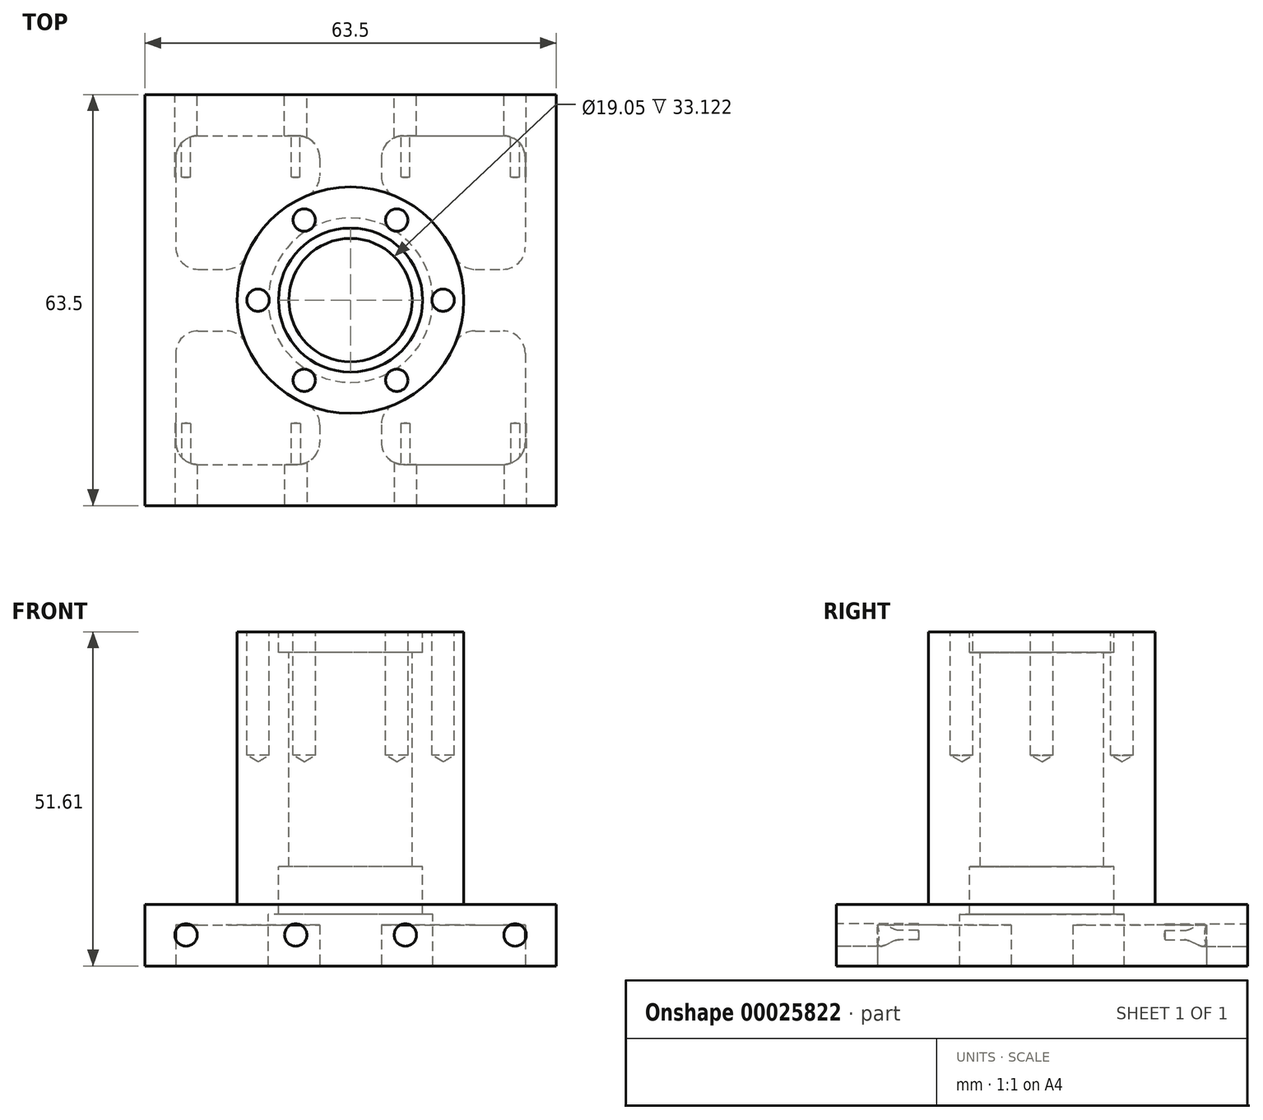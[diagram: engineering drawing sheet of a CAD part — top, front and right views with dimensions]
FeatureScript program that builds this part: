
annotation { "Feature Type Name" : "Feature", "Feature Type Description" : "" }
export const myFeature = defineFeature(function(context is Context, id is Id, definition is map)
    precondition{}
    {
        {
            var Q0;
            Q0=qCreatedBy(makeId("Front.planeOp"),FACE);
            var sketch = newSketch(context, id + "F0", { "sketchPlane" : qUnion([Q0])});
            skLineSegment(sketch, "E0", {"start": v(0, 39.17) * mm, "end": v(0, 0) * mm, "construction": true});
            skLineSegment(sketch, "E1", {"start": v(0, 0) * mm, "end": v(-12.7, 0) * mm, "construction": true});
            skLineSegment(sketch, "E2.bottom", {"start": v(-12.7, 0) * mm, "end": v(-45.72, 0) * mm});
            skLineSegment(sketch, "E2.top", {"start": v(-11.13, 51.61) * mm, "end": v(-17.49, 51.61) * mm});
            skLineSegment(sketch, "E2.left", {"start": v(-9.52, 15.32) * mm, "end": v(-9.53, 48.44) * mm});
            skLineSegment(sketch, "E2.right", {"start": v(-45.72, 0) * mm, "end": v(-45.72, 9.52) * mm});
            skLineSegment(sketch, "E3.top", {"start": v(-11.13, 48.44) * mm, "end": v(-9.53, 48.44) * mm});
            skLineSegment(sketch, "E3.left", {"start": v(-11.13, 51.61) * mm, "end": v(-11.13, 48.44) * mm});
            skLineSegment(sketch, "E4.bottom", {"start": v(-9.53, 15.32) * mm, "end": v(-11.13, 15.32) * mm});
            skLineSegment(sketch, "E4.right", {"start": v(-12.7, 7.95) * mm, "end": v(-12.7, 0) * mm});
            skLineSegment(sketch, "E5.bottom", {"start": v(-11.13, 7.95) * mm, "end": v(-12.7, 7.95) * mm});
            skLineSegment(sketch, "E5.left", {"start": v(-11.13, 7.95) * mm, "end": v(-11.13, 15.32) * mm});
            skLineSegment(sketch, "E6.bottom", {"start": v(-17.49, 9.53) * mm, "end": v(-45.72, 9.52) * mm});
            skLineSegment(sketch, "E6.left", {"start": v(-17.49, 9.53) * mm, "end": v(-17.49, 51.61) * mm});
            skSolve(sketch);
        }
        {
            var Q0;
            Q0=makeQuery(id+"F0.imprint","IMPRINT",FACE,{"disambiguationData":[TD([[makeQuery(id+"F0.imprint","IMPRINT",EDGE,{"derivedFrom":sQuery(id+"F0.wireOp",EDGE,"E2.bottom")}),-1.0]])]});
            var Q1;
            Q1=sQuery(id+"F0.wireOp",EDGE,"E0");
            revolve(context, id + "F1", {"entities" : qUnion([Q0]), "axis" : qUnion([Q1]), "revolveType" : RevolveType.FULL});
        }
        {
            var Q0;
            Q0=makeQuery(id+"F1.opRevolve","SWEPT_FACE",FACE,{"disambiguationData":[OSD([sQuery(id+"F0.wireOp",EDGE,"E2.bottom")])]});
            var sketch = newSketch(context, id + "F2", { "sketchPlane" : qUnion([Q0])});
            skLineSegment(sketch, "E7.rect.bottom", {"start": v(31.75, 31.75) * mm, "end": v(-31.75, 31.75) * mm});
            skLineSegment(sketch, "E7.rect.top", {"start": v(31.75, -31.75) * mm, "end": v(-31.75, -31.75) * mm});
            skLineSegment(sketch, "E7.rect.left", {"start": v(31.75, 31.75) * mm, "end": v(31.75, -31.75) * mm});
            skLineSegment(sketch, "E7.rect.right", {"start": v(-31.75, 31.75) * mm, "end": v(-31.75, -31.75) * mm});
            skPoint(sketch, "E7.rect.middle", {"position": v(0, 0) * mm});
            skSolve(sketch);
        }
        {
            var Q0;
            Q0=makeQuery(id+"F2.imprint","IMPRINT",FACE,{"disambiguationData":[TD([[makeQuery(id+"F2.imprint","IMPRINT",EDGE,{"derivedFrom":sQuery(id+"F2.wireOp",EDGE,"E7.rect.bottom")}),-1.0]])]});
            extrude(context, id + "F3", {"entities" : qUnion([Q0]), "operationType" : NewBodyOperationType.REMOVE, "endBound" : BoundingType.THROUGH_ALL, "oppositeDirection" : true, "depth" : 25.4 * mm});
        }
        {
            var Q0;
            Q0=makeQuery(id+"F3.boolean.opBoolean","COPY",FACE,{"derivedFrom":makeQuery(id+"F3.opExtrude","SWEPT_FACE",FACE,{"disambiguationData":[OSD([sQuery(id+"F2.wireOp",EDGE,"E7.rect.bottom")])]})});
            var sketch = newSketch(context, id + "F4", { "sketchPlane" : qUnion([Q0])});
            skLineSegment(sketch, "E8", {"start": v(-25.4, 4.78) * mm, "end": v(25.4, 4.78) * mm});
            skPoint(sketch, "E9", {"position": v(-8.47, 4.78) * mm});
            skPoint(sketch, "E10", {"position": v(8.47, 4.78) * mm});
            skLineSegment(sketch, "E11", {"start": v(0, 9.52) * mm, "end": v(0, -11.62) * mm});
            skSolve(sketch);
        }
        {
            var Q0;
            Q0=sQuery(id+"F4.wireOp",VERTEX,"E8.start");
            var Q1;
            Q1=sQuery(id+"F4.wireOp",VERTEX,"E9");
            var Q2;
            Q2=sQuery(id+"F4.wireOp",VERTEX,"E10");
            var Q3;
            Q3=sQuery(id+"F4.wireOp",VERTEX,"E8.end");
            var Q4;
            Q4=makeQuery(id+"F1.opRevolve","SWEPT_BODY",BODY,{"disambiguationData":[OSD([sQuery(id+"F0.wireOp",EDGE,"E2.bottom"),sQuery(id+"F0.wireOp",EDGE,"E2.top"),sQuery(id+"F0.wireOp",EDGE,"E2.left"),sQuery(id+"F0.wireOp",EDGE,"E2.right"),sQuery(id+"F0.wireOp",EDGE,"E3.top"),sQuery(id+"F0.wireOp",EDGE,"E3.left"),sQuery(id+"F0.wireOp",EDGE,"E4.bottom"),sQuery(id+"F0.wireOp",EDGE,"E4.right"),sQuery(id+"F0.wireOp",EDGE,"E5.bottom"),sQuery(id+"F0.wireOp",EDGE,"E5.left"),sQuery(id+"F0.wireOp",EDGE,"E6.bottom"),sQuery(id+"F0.wireOp",EDGE,"E6.left")])]});
            hole(context, id + "F5", {"style" : HoleStyle.SIMPLE, "holeDiameter" : 3.45 * mm, "endStyle" : HoleEndStyle.BLIND, "holeDepth" : 12.7 * mm, "locations" : qUnion([Q0, Q1, Q2, Q3]), "scope" : qUnion([Q4])});
        }
        {
            var Q0;
            Q0=makeQuery(id+"F1.opRevolve","SWEPT_FACE",FACE,{"disambiguationData":[OSD([sQuery(id+"F0.wireOp",EDGE,"E2.top")])]});
            var sketch = newSketch(context, id + "F6", { "sketchPlane" : qUnion([Q0])});
            skLineSegment(sketch, "E12", {"start": v(0, 0) * mm, "end": v(14.29, 0) * mm});
            skLineSegment(sketch, "E13.1.0", {"start": v(0, 0) * mm, "end": v(7.14, 12.37) * mm});
            skLineSegment(sketch, "E13.2.0", {"start": v(0, 0) * mm, "end": v(-7.14, 12.37) * mm});
            skLineSegment(sketch, "E13.3.0", {"start": v(0, 0) * mm, "end": v(-14.29, 0) * mm});
            skLineSegment(sketch, "E13.4.0", {"start": v(0, 0) * mm, "end": v(-7.14, -12.37) * mm});
            skLineSegment(sketch, "E13.5.0", {"start": v(0, 0) * mm, "end": v(7.14, -12.37) * mm});
            skPoint(sketch, "E13.center", {"position": v(0, 0) * mm});
            skSolve(sketch);
        }
        {
            var Q0;
            Q0=sQuery(id+"F6.wireOp",VERTEX,"E12.end");
            var Q1;
            Q1=sQuery(id+"F6.wireOp",VERTEX,"E13.5.0.end");
            var Q2;
            Q2=sQuery(id+"F6.wireOp",VERTEX,"E13.4.0.end");
            var Q3;
            Q3=sQuery(id+"F6.wireOp",VERTEX,"E13.3.0.end");
            var Q4;
            Q4=sQuery(id+"F6.wireOp",VERTEX,"E13.2.0.end");
            var Q5;
            Q5=sQuery(id+"F6.wireOp",VERTEX,"E13.1.0.end");
            var Q6;
            Q6=makeQuery(id+"F1.opRevolve","SWEPT_BODY",BODY,{"disambiguationData":[OSD([sQuery(id+"F0.wireOp",EDGE,"E2.bottom"),sQuery(id+"F0.wireOp",EDGE,"E2.top"),sQuery(id+"F0.wireOp",EDGE,"E2.left"),sQuery(id+"F0.wireOp",EDGE,"E2.right"),sQuery(id+"F0.wireOp",EDGE,"E3.top"),sQuery(id+"F0.wireOp",EDGE,"E3.left"),sQuery(id+"F0.wireOp",EDGE,"E4.bottom"),sQuery(id+"F0.wireOp",EDGE,"E4.right"),sQuery(id+"F0.wireOp",EDGE,"E5.bottom"),sQuery(id+"F0.wireOp",EDGE,"E5.left"),sQuery(id+"F0.wireOp",EDGE,"E6.bottom"),sQuery(id+"F0.wireOp",EDGE,"E6.left")])]});
            hole(context, id + "F7", {"style" : HoleStyle.SIMPLE, "holeDiameter" : 3.45 * mm, "endStyle" : HoleEndStyle.BLIND, "holeDepth" : 19.05 * mm, "locations" : qUnion([Q0, Q1, Q2, Q3, Q4, Q5]), "scope" : qUnion([Q6])});
        }
        {
            var Q0;
            Q0=makeQuery(id+"F1.opRevolve","SWEPT_FACE",FACE,{"disambiguationData":[OSD([sQuery(id+"F0.wireOp",EDGE,"E2.bottom")])]});
            var sketch = newSketch(context, id + "F8", { "sketchPlane" : qUnion([Q0])});
            skLineSegment(sketch, "E14.rect.bottom", {"start": v(-26.97, -25.4) * mm, "end": v(-4.76, -25.4) * mm});
            skLineSegment(sketch, "E14.rect.top", {"start": v(-26.97, 25.4) * mm, "end": v(-4.76, 25.4) * mm});
            skLineSegment(sketch, "E14.rect.left", {"start": v(-26.97, -25.4) * mm, "end": v(-26.97, -4.76) * mm});
            skLineSegment(sketch, "E14.rect.right", {"start": v(26.97, -25.4) * mm, "end": v(26.97, -4.76) * mm});
            skPoint(sketch, "E14.rect.middle", {"position": v(0, 0) * mm});
            skArc(sketch, "E15", {"start": v(-4.76, 16.81) * mm, "mid": v(-12.36, 12.36) * mm, "end": v(-16.81, 4.76) * mm});
            skLineSegment(sketch, "E16", {"start": v(-33.58, 0) * mm, "end": v(0, 0) * mm, "construction": true});
            skLineSegment(sketch, "E17", {"start": v(0, 36.76) * mm, "end": v(0, 0) * mm, "construction": true});
            skLineSegment(sketch, "E18.bottom", {"start": v(-26.97, -4.76) * mm, "end": v(-16.81, -4.76) * mm});
            skLineSegment(sketch, "E18.top", {"start": v(-26.97, 4.76) * mm, "end": v(-16.81, 4.76) * mm});
            skLineSegment(sketch, "E19.left", {"start": v(-4.76, 16.81) * mm, "end": v(-4.76, 25.4) * mm});
            skLineSegment(sketch, "E19.right", {"start": v(4.76, 16.81) * mm, "end": v(4.76, 25.4) * mm});
            skLineSegment(sketch, "E20.bottom", {"start": v(16.81, 4.76) * mm, "end": v(26.97, 4.76) * mm});
            skLineSegment(sketch, "E20.top", {"start": v(16.81, -4.76) * mm, "end": v(26.97, -4.76) * mm});
            skLineSegment(sketch, "E21.left", {"start": v(-4.76, -25.4) * mm, "end": v(-4.76, -16.81) * mm});
            skLineSegment(sketch, "E21.right", {"start": v(4.76, -25.4) * mm, "end": v(4.76, -16.81) * mm});
            skLineSegment(sketch, "E22.trimOffspring", {"start": v(4.76, 25.4) * mm, "end": v(26.97, 25.4) * mm});
            skArc(sketch, "E23.trimOffspring", {"start": v(16.81, 4.76) * mm, "mid": v(12.36, 12.36) * mm, "end": v(4.76, 16.81) * mm});
            skLineSegment(sketch, "E24.trimOffspring", {"start": v(4.76, -25.4) * mm, "end": v(26.97, -25.4) * mm});
            skArc(sketch, "E25.trimOffspring", {"start": v(4.76, -16.81) * mm, "mid": v(12.36, -12.36) * mm, "end": v(16.81, -4.76) * mm});
            skLineSegment(sketch, "E26.trimOffspring", {"start": v(-26.97, 4.76) * mm, "end": v(-26.97, 25.4) * mm});
            skArc(sketch, "E27.trimOffspring", {"start": v(-16.81, -4.76) * mm, "mid": v(-12.36, -12.36) * mm, "end": v(-4.76, -16.81) * mm});
            skLineSegment(sketch, "E28.trimOffspring", {"start": v(26.97, 4.76) * mm, "end": v(26.97, 25.4) * mm});
            skSolve(sketch);
        }
        {
            var Q0;
            Q0=makeQuery(id+"F8.imprint","IMPRINT",FACE,{"disambiguationData":[TD([[makeQuery(id+"F8.imprint","IMPRINT",EDGE,{"derivedFrom":sQuery(id+"F8.wireOp",EDGE,"E14.rect.bottom")}),1.0]])]});
            var Q1;
            Q1=makeQuery(id+"F8.imprint","IMPRINT",FACE,{"disambiguationData":[TD([[makeQuery(id+"F8.imprint","IMPRINT",EDGE,{"derivedFrom":sQuery(id+"F8.wireOp",EDGE,"E14.rect.top")}),-1.0]])]});
            var Q2;
            Q2=makeQuery(id+"F8.imprint","IMPRINT",FACE,{"disambiguationData":[TD([[makeQuery(id+"F8.imprint","IMPRINT",EDGE,{"derivedFrom":sQuery(id+"F8.wireOp",EDGE,"E19.right")}),-1.0]])]});
            var Q3;
            Q3=makeQuery(id+"F8.imprint","IMPRINT",FACE,{"disambiguationData":[TD([[makeQuery(id+"F8.imprint","IMPRINT",EDGE,{"derivedFrom":sQuery(id+"F8.wireOp",EDGE,"E14.rect.right")}),1.0]])]});
            extrude(context, id + "F9", {"entities" : qUnion([Q0, Q1, Q2, Q3]), "operationType" : NewBodyOperationType.REMOVE, "oppositeDirection" : true, "depth" : 6.35 * mm});
        }
        {
            var Q0;
            Q0=makeQuery(id+"F9.boolean.opBoolean","COPY",EDGE,{"derivedFrom":makeQuery(id+"F9.opExtrude","SWEPT_EDGE",EDGE,{"disambiguationData":[OSD([sQuery(id+"F8.wireOp",EDGE,"E14.rect.bottom"),sQuery(id+"F8.wireOp",EDGE,"E21.left")])]})});
            var Q1;
            Q1=makeQuery(id+"F9.boolean.opBoolean","COPY",EDGE,{"derivedFrom":makeQuery(id+"F9.opExtrude","SWEPT_EDGE",EDGE,{"disambiguationData":[OSD([sQuery(id+"F8.wireOp",EDGE,"E21.left"),sQuery(id+"F8.wireOp",EDGE,"E27.trimOffspring")])]})});
            var Q2;
            Q2=makeQuery(id+"F9.boolean.opBoolean","COPY",EDGE,{"derivedFrom":makeQuery(id+"F9.opExtrude","SWEPT_EDGE",EDGE,{"disambiguationData":[OSD([sQuery(id+"F8.wireOp",EDGE,"E18.bottom"),sQuery(id+"F8.wireOp",EDGE,"E27.trimOffspring")])]})});
            var Q3;
            Q3=makeQuery(id+"F9.boolean.opBoolean","COPY",EDGE,{"derivedFrom":makeQuery(id+"F9.opExtrude","SWEPT_EDGE",EDGE,{"disambiguationData":[OSD([sQuery(id+"F8.wireOp",EDGE,"E14.rect.left"),sQuery(id+"F8.wireOp",EDGE,"E18.bottom")])]})});
            var Q4;
            Q4=makeQuery(id+"F9.boolean.opBoolean","COPY",EDGE,{"derivedFrom":makeQuery(id+"F9.opExtrude","SWEPT_EDGE",EDGE,{"disambiguationData":[OSD([sQuery(id+"F8.wireOp",EDGE,"E14.rect.bottom"),sQuery(id+"F8.wireOp",EDGE,"E14.rect.left")])]})});
            var Q5;
            Q5=makeQuery(id+"F9.boolean.opBoolean","COPY",EDGE,{"derivedFrom":makeQuery(id+"F9.opExtrude","SWEPT_EDGE",EDGE,{"disambiguationData":[OSD([sQuery(id+"F8.wireOp",EDGE,"E18.top"),sQuery(id+"F8.wireOp",EDGE,"E26.trimOffspring")])]})});
            var Q6;
            Q6=makeQuery(id+"F9.boolean.opBoolean","COPY",EDGE,{"derivedFrom":makeQuery(id+"F9.opExtrude","SWEPT_EDGE",EDGE,{"disambiguationData":[OSD([sQuery(id+"F8.wireOp",EDGE,"E21.right"),sQuery(id+"F8.wireOp",EDGE,"E24.trimOffspring")])]})});
            var Q7;
            Q7=makeQuery(id+"F9.boolean.opBoolean","COPY",EDGE,{"derivedFrom":makeQuery(id+"F9.opExtrude","SWEPT_EDGE",EDGE,{"disambiguationData":[OSD([sQuery(id+"F8.wireOp",EDGE,"E20.bottom"),sQuery(id+"F8.wireOp",EDGE,"E23.trimOffspring")])]})});
            var Q8;
            Q8=makeQuery(id+"F9.boolean.opBoolean","COPY",EDGE,{"derivedFrom":makeQuery(id+"F9.opExtrude","SWEPT_EDGE",EDGE,{"disambiguationData":[OSD([sQuery(id+"F8.wireOp",EDGE,"E19.right"),sQuery(id+"F8.wireOp",EDGE,"E23.trimOffspring")])]})});
            var Q9;
            Q9=makeQuery(id+"F9.boolean.opBoolean","COPY",EDGE,{"derivedFrom":makeQuery(id+"F9.opExtrude","SWEPT_EDGE",EDGE,{"disambiguationData":[OSD([sQuery(id+"F8.wireOp",EDGE,"E15"),sQuery(id+"F8.wireOp",EDGE,"E19.left")])]})});
            var Q10;
            Q10=makeQuery(id+"F9.boolean.opBoolean","COPY",EDGE,{"derivedFrom":makeQuery(id+"F9.opExtrude","SWEPT_EDGE",EDGE,{"disambiguationData":[OSD([sQuery(id+"F8.wireOp",EDGE,"E15"),sQuery(id+"F8.wireOp",EDGE,"E18.top")])]})});
            var Q11;
            Q11=makeQuery(id+"F9.boolean.opBoolean","COPY",EDGE,{"derivedFrom":makeQuery(id+"F9.opExtrude","SWEPT_EDGE",EDGE,{"disambiguationData":[OSD([sQuery(id+"F8.wireOp",EDGE,"E14.rect.right"),sQuery(id+"F8.wireOp",EDGE,"E24.trimOffspring")])]})});
            var Q12;
            Q12=makeQuery(id+"F9.boolean.opBoolean","COPY",EDGE,{"derivedFrom":makeQuery(id+"F9.opExtrude","SWEPT_EDGE",EDGE,{"disambiguationData":[OSD([sQuery(id+"F8.wireOp",EDGE,"E20.bottom"),sQuery(id+"F8.wireOp",EDGE,"E28.trimOffspring")])]})});
            var Q13;
            Q13=makeQuery(id+"F9.boolean.opBoolean","COPY",EDGE,{"disambiguationData":[OD(0.0)],"derivedFrom":makeQuery(id+"F9.opExtrude","SWEPT_EDGE",EDGE,{"disambiguationData":[OSD([sQuery(id+"F8.wireOp",EDGE,"E14.rect.top"),sQuery(id+"F8.wireOp",EDGE,"E26.trimOffspring")])]})});
            var Q14;
            Q14=makeQuery(id+"F9.boolean.opBoolean","COPY",EDGE,{"derivedFrom":makeQuery(id+"F9.opExtrude","SWEPT_EDGE",EDGE,{"disambiguationData":[OSD([sQuery(id+"F8.wireOp",EDGE,"E14.rect.top"),sQuery(id+"F8.wireOp",EDGE,"E19.left")])]})});
            var Q15;
            Q15=makeQuery(id+"F9.boolean.opBoolean","COPY",EDGE,{"disambiguationData":[OD(0.0)],"derivedFrom":makeQuery(id+"F9.opExtrude","SWEPT_EDGE",EDGE,{"disambiguationData":[OSD([sQuery(id+"F8.wireOp",EDGE,"E22.trimOffspring"),sQuery(id+"F8.wireOp",EDGE,"E28.trimOffspring")])]})});
            var Q16;
            Q16=makeQuery(id+"F9.boolean.opBoolean","COPY",EDGE,{"derivedFrom":makeQuery(id+"F9.opExtrude","SWEPT_EDGE",EDGE,{"disambiguationData":[OSD([sQuery(id+"F8.wireOp",EDGE,"E19.right"),sQuery(id+"F8.wireOp",EDGE,"E22.trimOffspring")])]})});
            var Q17;
            Q17=makeQuery(id+"F9.boolean.opBoolean","COPY",EDGE,{"derivedFrom":makeQuery(id+"F9.opExtrude","SWEPT_EDGE",EDGE,{"disambiguationData":[OSD([sQuery(id+"F8.wireOp",EDGE,"E20.top"),sQuery(id+"F8.wireOp",EDGE,"E25.trimOffspring")])]})});
            var Q18;
            Q18=makeQuery(id+"F9.boolean.opBoolean","COPY",EDGE,{"derivedFrom":makeQuery(id+"F9.opExtrude","SWEPT_EDGE",EDGE,{"disambiguationData":[OSD([sQuery(id+"F8.wireOp",EDGE,"E21.right"),sQuery(id+"F8.wireOp",EDGE,"E25.trimOffspring")])]})});
            var Q19;
            Q19=makeQuery(id+"F9.boolean.opBoolean","COPY",EDGE,{"derivedFrom":makeQuery(id+"F9.opExtrude","SWEPT_EDGE",EDGE,{"disambiguationData":[OSD([sQuery(id+"F8.wireOp",EDGE,"E14.rect.right"),sQuery(id+"F8.wireOp",EDGE,"E20.top")])]})});
            fillet(context, id + "F10", {"entities" : qUnion([Q0, Q1, Q2, Q3, Q4, Q5, Q6, Q7, Q8, Q9, Q10, Q11, Q12, Q13, Q14, Q15, Q16, Q17, Q18, Q19]), "radius" : 3.43 * mm, "tangentPropagation" : true, "allowEdgeOverflow" : false});
        }
        {
            var Q0;
            Q0=makeQuery(id+"F3.boolean.opBoolean","COPY",FACE,{"derivedFrom":makeQuery(id+"F3.opExtrude","SWEPT_FACE",FACE,{"disambiguationData":[OSD([sQuery(id+"F2.wireOp",EDGE,"E7.rect.top")])]})});
            var sketch = newSketch(context, id + "F11", { "sketchPlane" : qUnion([Q0])});
            skLineSegment(sketch, "E29", {"start": v(-25.4, 4.76) * mm, "end": v(25.4, 4.76) * mm});
            skPoint(sketch, "E30", {"position": v(-8.47, 4.76) * mm});
            skPoint(sketch, "E31", {"position": v(8.47, 4.76) * mm});
            skLineSegment(sketch, "E32", {"start": v(0, 9.52) * mm, "end": v(0, -12.08) * mm});
            skSolve(sketch);
        }
        {
            var Q0;
            Q0=sQuery(id+"F11.wireOp",VERTEX,"E29.start");
            var Q1;
            Q1=sQuery(id+"F11.wireOp",VERTEX,"E30");
            var Q2;
            Q2=sQuery(id+"F11.wireOp",VERTEX,"E31");
            var Q3;
            Q3=sQuery(id+"F11.wireOp",VERTEX,"E29.end");
            var Q4;
            Q4=makeQuery(id+"F1.opRevolve","SWEPT_BODY",BODY,{"disambiguationData":[OSD([sQuery(id+"F0.wireOp",EDGE,"E2.bottom"),sQuery(id+"F0.wireOp",EDGE,"E2.top"),sQuery(id+"F0.wireOp",EDGE,"E2.left"),sQuery(id+"F0.wireOp",EDGE,"E2.right"),sQuery(id+"F0.wireOp",EDGE,"E3.top"),sQuery(id+"F0.wireOp",EDGE,"E3.left"),sQuery(id+"F0.wireOp",EDGE,"E4.bottom"),sQuery(id+"F0.wireOp",EDGE,"E4.right"),sQuery(id+"F0.wireOp",EDGE,"E5.bottom"),sQuery(id+"F0.wireOp",EDGE,"E5.left"),sQuery(id+"F0.wireOp",EDGE,"E6.bottom"),sQuery(id+"F0.wireOp",EDGE,"E6.left")])]});
            hole(context, id + "F12", {"style" : HoleStyle.SIMPLE, "holeDiameter" : 3.45 * mm, "endStyle" : HoleEndStyle.BLIND, "holeDepth" : 12.7 * mm, "locations" : qUnion([Q0, Q1, Q2, Q3]), "scope" : qUnion([Q4])});
        }
    });
